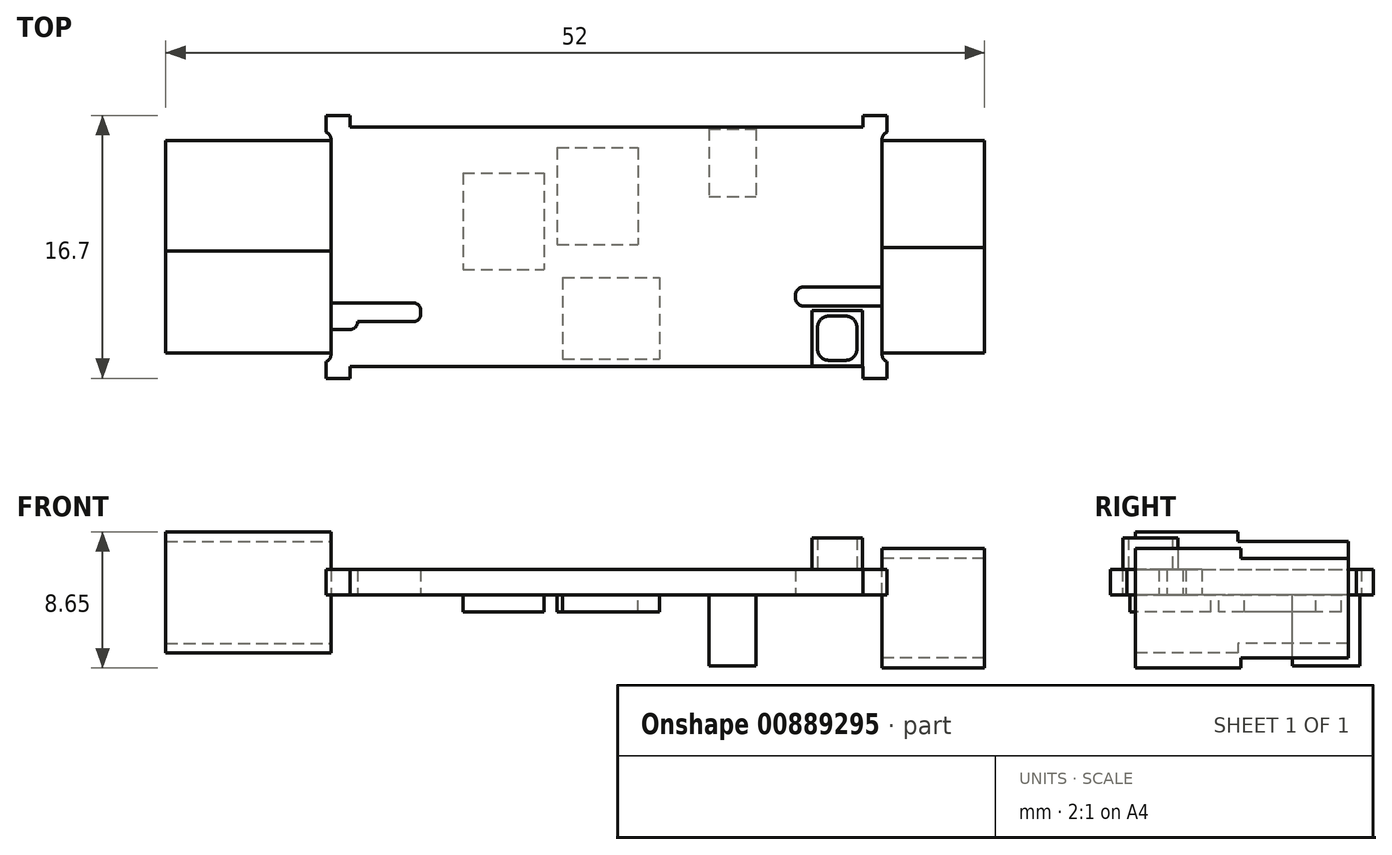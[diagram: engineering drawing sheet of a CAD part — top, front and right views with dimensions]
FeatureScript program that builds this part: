
annotation { "Feature Type Name" : "Feature", "Feature Type Description" : "" }
export const myFeature = defineFeature(function(context is Context, id is Id, definition is map)
    precondition{}
    {
        {
            var Q0;
            Q0=qCreatedBy(makeId("Top.planeOp"),FACE);
            var sketch = newSketch(context, id + "F0", { "sketchPlane" : qUnion([Q0])});
            skLineSegment(sketch, "E0", {"start": v(0.77, 15.2) * mm, "end": v(34.23, 15.2) * mm});
            skLineSegment(sketch, "E1", {"start": v(35, 14.43) * mm, "end": v(35, 5.05) * mm});
            skLineSegment(sketch, "E2", {"start": v(35, 5.05) * mm, "end": v(30, 5.05) * mm});
            skLineSegment(sketch, "E3", {"start": v(29.5, 4.55) * mm, "end": v(29.5, 4.35) * mm});
            skLineSegment(sketch, "E4", {"start": v(30, 3.85) * mm, "end": v(35, 3.85) * mm});
            skLineSegment(sketch, "E5", {"start": v(35, 3.85) * mm, "end": v(35, 0.77) * mm});
            skLineSegment(sketch, "E6", {"start": v(34.23, 0) * mm, "end": v(0.77, 0) * mm});
            skLineSegment(sketch, "E7", {"start": v(0, 0.77) * mm, "end": v(0, 2.35) * mm});
            skLineSegment(sketch, "E8", {"start": v(0, 2.35) * mm, "end": v(1.2, 2.35) * mm});
            skLineSegment(sketch, "E9", {"start": v(1.7, 2.85) * mm, "end": v(5.2, 2.85) * mm});
            skLineSegment(sketch, "E10", {"start": v(5.7, 3.35) * mm, "end": v(5.7, 3.55) * mm});
            skLineSegment(sketch, "E11", {"start": v(5.2, 4.05) * mm, "end": v(0, 4.05) * mm});
            skLineSegment(sketch, "E12", {"start": v(0, 4.05) * mm, "end": v(0, 14.43) * mm});
            skArc(sketch, "E13", {"start": v(5.7, 3.55) * mm, "mid": v(5.55, 3.9) * mm, "end": v(5.2, 4.05) * mm});
            skArc(sketch, "E14", {"start": v(5.2, 2.85) * mm, "mid": v(5.55, 3) * mm, "end": v(5.7, 3.35) * mm});
            skArc(sketch, "E15", {"start": v(1.2, 2.35) * mm, "mid": v(1.55, 2.5) * mm, "end": v(1.7, 2.85) * mm});
            skArc(sketch, "E16", {"start": v(29.5, 4.35) * mm, "mid": v(29.65, 4) * mm, "end": v(30, 3.85) * mm});
            skArc(sketch, "E17", {"start": v(30, 5.05) * mm, "mid": v(29.65, 4.9) * mm, "end": v(29.5, 4.55) * mm});
            skPoint(sketch, "E18.orphan", {"position": v(0, 0) * mm});
            skArc(sketch, "E19", {"start": v(34.69, -0.31) * mm, "mid": v(34.5, -0.08) * mm, "end": v(34.23, 0) * mm});
            skArc(sketch, "E20", {"start": v(35, 0.77) * mm, "mid": v(35.08, 0.5) * mm, "end": v(35.31, 0.31) * mm});
            skLineSegment(sketch, "E21", {"start": v(31.97, 3.03) * mm, "end": v(38.74, -3.74) * mm, "construction": true});
            skPoint(sketch, "E22", {"position": v(35, 0) * mm});
            skLineSegment(sketch, "E23", {"start": v(35.31, 0.31) * mm, "end": v(34.69, -0.31) * mm});
            skLineSegment(sketch, "E24", {"start": v(-1.2, -1.2) * mm, "end": v(1.9, 1.9) * mm, "construction": true});
            skArc(sketch, "E25", {"start": v(0.77, 0) * mm, "mid": v(0.5, -0.08) * mm, "end": v(0.31, -0.31) * mm});
            skArc(sketch, "E26", {"start": v(-0.31, 0.31) * mm, "mid": v(-0.08, 0.5) * mm, "end": v(0, 0.77) * mm});
            skLineSegment(sketch, "E27", {"start": v(-0.31, 0.31) * mm, "end": v(0.31, -0.31) * mm});
            skPoint(sketch, "E28", {"position": v(35, 15.2) * mm});
            skLineSegment(sketch, "E29", {"start": v(32, 12.2) * mm, "end": v(37.84, 18.04) * mm, "construction": true});
            skArc(sketch, "E30", {"start": v(34.23, 15.2) * mm, "mid": v(34.5, 15.28) * mm, "end": v(34.69, 15.51) * mm});
            skArc(sketch, "E31", {"start": v(35.31, 14.89) * mm, "mid": v(35.08, 14.7) * mm, "end": v(35, 14.43) * mm});
            skLineSegment(sketch, "E32", {"start": v(34.69, 15.51) * mm, "end": v(35.31, 14.89) * mm});
            skPoint(sketch, "E33", {"position": v(0, 15.2) * mm});
            skLineSegment(sketch, "E34", {"start": v(-2.33, 17.53) * mm, "end": v(2.44, 12.76) * mm, "construction": true});
            skArc(sketch, "E35", {"start": v(0, 14.43) * mm, "mid": v(-0.08, 14.7) * mm, "end": v(-0.31, 14.89) * mm});
            skArc(sketch, "E36", {"start": v(0.31, 15.51) * mm, "mid": v(0.5, 15.28) * mm, "end": v(0.77, 15.2) * mm});
            skLineSegment(sketch, "E37", {"start": v(-0.31, 14.89) * mm, "end": v(0.31, 15.51) * mm});
            skLineSegment(sketch, "E38", {"start": v(-0.31, 14.89) * mm, "end": v(-0.31, 15.95) * mm});
            skLineSegment(sketch, "E39", {"start": v(-0.31, 15.95) * mm, "end": v(1.2, 15.95) * mm});
            skLineSegment(sketch, "E40", {"start": v(1.2, 15.95) * mm, "end": v(1.2, 15.2) * mm});
            skLineSegment(sketch, "E41", {"start": v(35.31, 14.89) * mm, "end": v(35.31, 15.95) * mm});
            skLineSegment(sketch, "E42", {"start": v(35.31, 15.95) * mm, "end": v(33.8, 15.95) * mm});
            skLineSegment(sketch, "E43", {"start": v(33.8, 15.95) * mm, "end": v(33.8, 15.2) * mm});
            skLineSegment(sketch, "E44", {"start": v(-0.31, 0.31) * mm, "end": v(-0.31, -0.75) * mm});
            skLineSegment(sketch, "E45", {"start": v(-0.31, -0.75) * mm, "end": v(1.2, -0.75) * mm});
            skLineSegment(sketch, "E46", {"start": v(1.2, -0.75) * mm, "end": v(1.2, 0) * mm});
            skLineSegment(sketch, "E47", {"start": v(35.31, 0.31) * mm, "end": v(35.31, -0.75) * mm});
            skLineSegment(sketch, "E48", {"start": v(35.31, -0.75) * mm, "end": v(33.8, -0.75) * mm});
            skLineSegment(sketch, "E49", {"start": v(33.8, -0.75) * mm, "end": v(33.8, 0) * mm});
            skSolve(sketch);
        }
        {
            var Q0;
            Q0 = qSketchRegion(id + "F0", true);
            extrude(context, id + "F1", {"entities" : qUnion([Q0]), "depth" : 1.6 * mm, "offsetDistance" : 25 * mm});
        }
        {
            var Q0;
            Q0=qCreatedBy(makeId("Right.planeOp"),FACE);
            var sketch = newSketch(context, id + "F2", { "sketchPlane" : qUnion([Q0])});
            skLineSegment(sketch, "E50", {"start": v(0.85, 4) * mm, "end": v(7.35, 4) * mm});
            skLineSegment(sketch, "E51", {"start": v(7.35, 4) * mm, "end": v(7.35, 3.4) * mm});
            skLineSegment(sketch, "E52", {"start": v(7.35, 3.4) * mm, "end": v(14.35, 3.4) * mm});
            skLineSegment(sketch, "E53", {"start": v(14.35, 3.4) * mm, "end": v(14.35, -3.1) * mm});
            skLineSegment(sketch, "E54", {"start": v(14.35, -3.1) * mm, "end": v(7.35, -3.1) * mm});
            skLineSegment(sketch, "E55", {"start": v(7.35, -3.1) * mm, "end": v(7.35, -3.7) * mm});
            skLineSegment(sketch, "E56", {"start": v(7.35, -3.7) * mm, "end": v(0.85, -3.7) * mm});
            skLineSegment(sketch, "E57", {"start": v(0.85, -3.7) * mm, "end": v(0.85, 4) * mm});
            skSolve(sketch);
        }
        {
            var Q0;
            Q0 = qSketchRegion(id + "F2", true);
            extrude(context, id + "F3", {"entities" : qUnion([Q0]), "operationType" : NewBodyOperationType.ADD, "oppositeDirection" : true, "depth" : 10.5 * mm, "offsetDistance" : 25 * mm});
        }
        {
            var Q0;
            Q0=qCreatedBy(makeId("Right.planeOp"),FACE);
            var sketch = newSketch(context, id + "F4", { "sketchPlane" : qUnion([Q0])});
            skLineSegment(sketch, "E58", {"start": v(0.85, 2.95) * mm, "end": v(7.55, 2.95) * mm});
            skLineSegment(sketch, "E59", {"start": v(7.55, 2.95) * mm, "end": v(7.55, 2.3) * mm});
            skLineSegment(sketch, "E60", {"start": v(7.55, 2.3) * mm, "end": v(14.35, 2.3) * mm});
            skLineSegment(sketch, "E61", {"start": v(14.35, 2.3) * mm, "end": v(14.35, -4) * mm});
            skLineSegment(sketch, "E62", {"start": v(14.35, -4) * mm, "end": v(7.55, -4) * mm});
            skLineSegment(sketch, "E63", {"start": v(7.55, -4) * mm, "end": v(7.55, -4.65) * mm});
            skLineSegment(sketch, "E64", {"start": v(7.55, -4.65) * mm, "end": v(0.85, -4.65) * mm});
            skLineSegment(sketch, "E65", {"start": v(0.85, -4.65) * mm, "end": v(0.85, 2.95) * mm});
            skSolve(sketch);
        }
        {
            var Q0;
            Q0 = qSketchRegion(id + "F4", true);
            extrude(context, id + "F5", {"entities" : qUnion([Q0]), "operationType" : NewBodyOperationType.ADD, "depth" : 41.5 * mm, "offsetDistance" : 25 * mm, "hasSecondDirection" : true, "secondDirectionOppositeDirection" : false, "secondDirectionDepth" : 35 * mm});
        }
        {
            var Q0;
            Q0=qCreatedBy(makeId("Top.planeOp"),FACE);
            var sketch = newSketch(context, id + "F6", { "sketchPlane" : qUnion([Q0])});
            skLineSegment(sketch, "E66.bottom", {"start": v(30.55, 3.55) * mm, "end": v(33.75, 3.55) * mm});
            skLineSegment(sketch, "E66.top", {"start": v(30.55, 0.05) * mm, "end": v(33.75, 0.05) * mm});
            skLineSegment(sketch, "E66.left", {"start": v(30.55, 3.55) * mm, "end": v(30.55, 0.05) * mm});
            skLineSegment(sketch, "E66.right", {"start": v(33.75, 3.55) * mm, "end": v(33.75, 0.05) * mm});
            skArc(sketch, "E67", {"start": v(31.6, 3.2) * mm, "mid": v(31.1, 3) * mm, "end": v(30.9, 2.5) * mm});
            skArc(sketch, "E68", {"start": v(33.4, 2.5) * mm, "mid": v(33.2, 3) * mm, "end": v(32.7, 3.2) * mm});
            skArc(sketch, "E69", {"start": v(30.9, 1.1) * mm, "mid": v(31.1, 0.6) * mm, "end": v(31.6, 0.4) * mm});
            skArc(sketch, "E70", {"start": v(32.7, 0.4) * mm, "mid": v(33.2, 0.6) * mm, "end": v(33.4, 1.1) * mm});
            skLineSegment(sketch, "E71", {"start": v(31.6, 0.4) * mm, "end": v(32.7, 0.4) * mm});
            skLineSegment(sketch, "E72", {"start": v(30.9, 1.1) * mm, "end": v(30.9, 2.5) * mm});
            skLineSegment(sketch, "E73", {"start": v(31.6, 3.2) * mm, "end": v(32.7, 3.2) * mm});
            skLineSegment(sketch, "E74", {"start": v(33.4, 2.5) * mm, "end": v(33.4, 1.1) * mm});
            skLineSegment(sketch, "E75", {"start": v(30.9, 2.5) * mm, "end": v(30.55, 2.5) * mm, "construction": true});
            skLineSegment(sketch, "E76", {"start": v(31.6, 3.2) * mm, "end": v(31.6, 3.55) * mm, "construction": true});
            skLineSegment(sketch, "E77", {"start": v(31.6, 0.4) * mm, "end": v(31.6, 0.05) * mm, "construction": true});
            skLineSegment(sketch, "E78", {"start": v(33.4, 2.5) * mm, "end": v(33.75, 2.5) * mm, "construction": true});
            skLineSegment(sketch, "E79", {"start": v(30.55, 3.55) * mm, "end": v(33.75, 0.05) * mm, "construction": true});
            skLineSegment(sketch, "E80", {"start": v(30.55, 0.05) * mm, "end": v(33.75, 3.55) * mm, "construction": true});
            skPoint(sketch, "E81", {"position": v(32.15, 1.8) * mm});
            skSolve(sketch);
        }
        {
            var Q0;
            Q0 = qSketchRegion(id + "F6", true);
            extrude(context, id + "F7", {"entities" : qUnion([Q0]), "operationType" : NewBodyOperationType.ADD, "depth" : (1.6 + 2) * mm, "offsetDistance" : 25 * mm});
        }
        {
            var Q0;
            Q0=qCreatedBy(makeId("Top.planeOp"),FACE);
            var sketch = newSketch(context, id + "F8", { "sketchPlane" : qUnion([Q0])});
            skLineSegment(sketch, "E82.bottom", {"start": v(24, 15.1) * mm, "end": v(27, 15.1) * mm});
            skLineSegment(sketch, "E82.top", {"start": v(24, 10.8) * mm, "end": v(27, 10.8) * mm});
            skLineSegment(sketch, "E82.left", {"start": v(24, 15.1) * mm, "end": v(24, 10.8) * mm});
            skLineSegment(sketch, "E82.right", {"start": v(27, 15.1) * mm, "end": v(27, 10.8) * mm});
            skSolve(sketch);
        }
        {
            var Q0;
            Q0 = qSketchRegion(id + "F8", true);
            extrude(context, id + "F9", {"entities" : qUnion([Q0]), "operationType" : NewBodyOperationType.ADD, "oppositeDirection" : true, "depth" : 4.5 * mm, "offsetDistance" : 25 * mm});
        }
        {
            var Q0;
            Q0=qCreatedBy(makeId("Top.planeOp"),FACE);
            var sketch = newSketch(context, id + "F10", { "sketchPlane" : qUnion([Q0])});
            skLineSegment(sketch, "E83.bottom", {"start": v(8.38, 12.3) * mm, "end": v(13.53, 12.3) * mm});
            skLineSegment(sketch, "E83.top", {"start": v(8.38, 6.16) * mm, "end": v(13.53, 6.16) * mm});
            skLineSegment(sketch, "E83.left", {"start": v(8.38, 12.3) * mm, "end": v(8.38, 6.16) * mm});
            skLineSegment(sketch, "E83.right", {"start": v(13.53, 12.3) * mm, "end": v(13.53, 6.16) * mm});
            skLineSegment(sketch, "E84.bottom", {"start": v(14.36, 13.9) * mm, "end": v(19.51, 13.9) * mm});
            skLineSegment(sketch, "E84.top", {"start": v(14.36, 7.76) * mm, "end": v(19.51, 7.76) * mm});
            skLineSegment(sketch, "E84.left", {"start": v(14.36, 13.9) * mm, "end": v(14.36, 7.76) * mm});
            skLineSegment(sketch, "E84.right", {"start": v(19.51, 13.9) * mm, "end": v(19.51, 7.76) * mm});
            skLineSegment(sketch, "E85.bottom", {"start": v(14.71, 5.64) * mm, "end": v(20.86, 5.64) * mm});
            skLineSegment(sketch, "E85.top", {"start": v(14.71, 0.5) * mm, "end": v(20.86, 0.5) * mm});
            skLineSegment(sketch, "E85.left", {"start": v(14.71, 5.64) * mm, "end": v(14.71, 0.5) * mm});
            skLineSegment(sketch, "E85.right", {"start": v(20.86, 5.64) * mm, "end": v(20.86, 0.5) * mm});
            skSolve(sketch);
        }
        {
            var Q0;
            Q0 = qSketchRegion(id + "F10", true);
            extrude(context, id + "F11", {"entities" : qUnion([Q0]), "operationType" : NewBodyOperationType.ADD, "oppositeDirection" : true, "depth" : 1.1 * mm, "offsetDistance" : 25 * mm});
        }
    });
